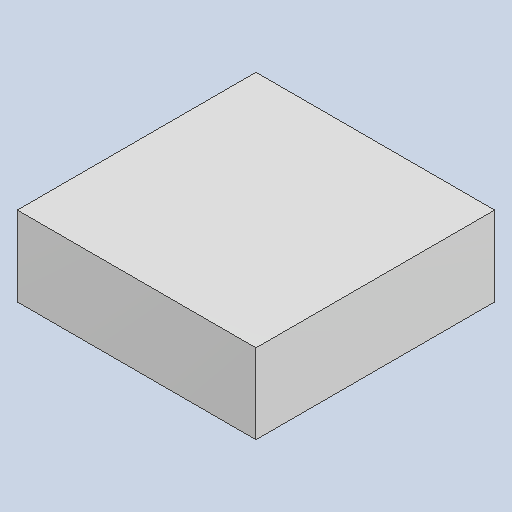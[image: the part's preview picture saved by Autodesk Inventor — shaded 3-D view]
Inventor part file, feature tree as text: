
AUTODESK INVENTOR PART (.ipt)
format: ipt  version: 2023.4 (Build 274418000, 418)  size: 79,872 bytes
history: native  units: mm
features: extrude x1
ambient origin geometry x8: Origin, YZ Plane, XZ Plane, XY Plane, X Axis, Y Axis, Z Axis, Center Point
bodies: Solid1 (feature_tree)
feature tree (1):
  extrude  "Extruded_26"  [1 undecoded]
note: 1 required parameter value undecoded (feature->parameter linkage not recoverable at this tier; creation-order binding heuristic only, values carry confidence <= 0.55)
